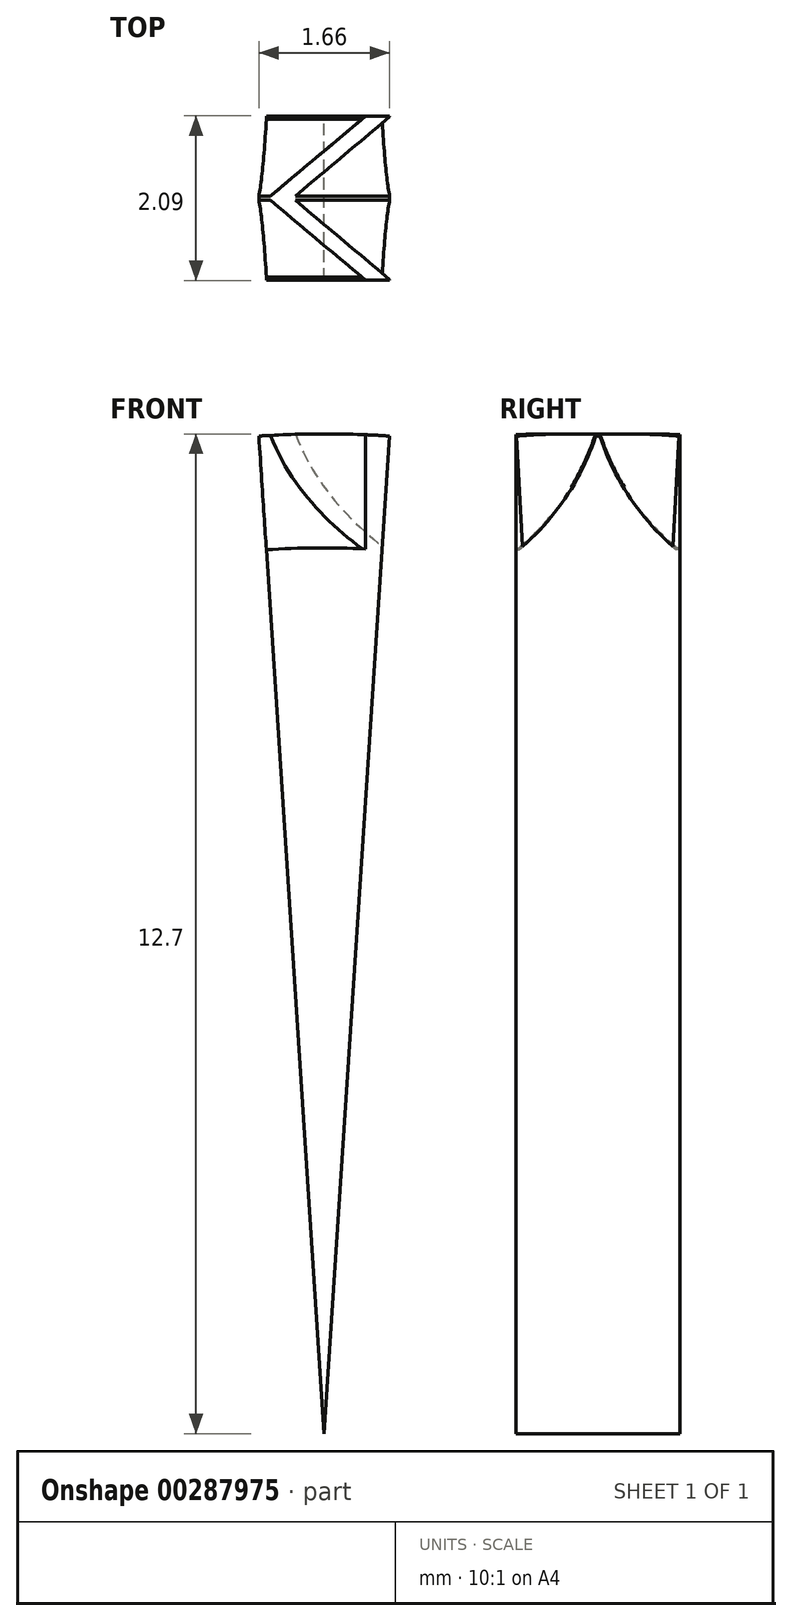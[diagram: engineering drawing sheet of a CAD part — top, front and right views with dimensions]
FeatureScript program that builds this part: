
annotation { "Feature Type Name" : "Feature", "Feature Type Description" : "" }
export const myFeature = defineFeature(function(context is Context, id is Id, definition is map)
    precondition{}
    {
        {
            var Q0;
            Q0=qCreatedBy(makeId("Front.planeOp"),FACE);
            var sketch = newSketch(context, id + "F0", { "sketchPlane" : qUnion([Q0])});
            skLineSegment(sketch, "E0", {"start": v(0, 0) * mm, "end": v(-0.88, 13.46) * mm});
            skLineSegment(sketch, "E1", {"start": v(0, 0) * mm, "end": v(0.88, 13.46) * mm});
            skLineSegment(sketch, "E2", {"start": v(-0.88, 13.46) * mm, "end": v(0.88, 13.46) * mm});
            skSolve(sketch);
        }
        {
            var Q0;
            Q0 = qSketchRegion(id + "F0", true);
            extrude(context, id + "F1", {"entities" : qUnion([Q0]), "depth" : 0.05 * mm, "offsetDistance" : 25.4 * mm});
        }
        {
            var Q0;
            Q0=makeQuery(id+"F1.opExtrude","SWEPT_FACE",FACE,{"disambiguationData":[OSD([sQuery(id+"F0.wireOp",EDGE,"E2")])]});
            var sketch = newSketch(context, id + "F2", { "sketchPlane" : qUnion([Q0])});
            skLineSegment(sketch, "E3", {"start": v(-0.69, 0) * mm, "end": v(0.53, 1.02) * mm});
            skLineSegment(sketch, "E4", {"start": v(0.84, 1.02) * mm, "end": v(-0.37, 0) * mm});
            skLineSegment(sketch, "E5", {"start": v(-0.69, -0.05) * mm, "end": v(0.53, -1.07) * mm});
            skLineSegment(sketch, "E6", {"start": v(0.84, -1.07) * mm, "end": v(-0.37, -0.05) * mm});
            skLineSegment(sketch, "E7", {"start": v(-0.69, 0) * mm, "end": v(-0.37, 0) * mm});
            skLineSegment(sketch, "E8", {"start": v(-0.69, 0) * mm, "end": v(-0.13, 0) * mm});
            skLineSegment(sketch, "E9", {"start": v(-0.37, -0.05) * mm, "end": v(-0.69, -0.05) * mm});
            skLineSegment(sketch, "E10", {"start": v(0.53, 1.02) * mm, "end": v(0.84, 1.02) * mm});
            skLineSegment(sketch, "E11", {"start": v(0.53, -1.07) * mm, "end": v(0.84, -1.07) * mm});
            skPoint(sketch, "E12.orphan", {"position": v(1.16, -1.07) * mm});
            skLineSegment(sketch, "E13", {"start": v(-0.69, 0) * mm, "end": v(-0.69, -0.05) * mm, "construction": true});
            skSolve(sketch);
        }
        {
            var Q0;
            Q0 = qSketchRegion(id + "F2", true);
            extrude(context, id + "F3", {"entities" : qUnion([Q0]), "operationType" : NewBodyOperationType.ADD, "oppositeDirection" : true, "depth" : 2.54 * mm, "offsetDistance" : 25.4 * mm});
        }
        {
            var Q0;
            {var subQ0=sQuery(id+"F0.wireOp",EDGE,"E2");var subQ1=sQuery(id+"F0.wireOp",EDGE,"E1");var subQ2=sQuery(id+"F0.wireOp",EDGE,"E0");var subQ3=makeQuery(id+"F1.opExtrude","CAP_FACE",FACE,{"disambiguationData":[OSD([subQ2,subQ1,subQ0])],"isStart":false});var subQ4=sQuery(id+"F2.wireOp",EDGE,"E5");var subQ5=sQuery(id+"F2.wireOp",EDGE,"E9");var subQ6=sQuery(id+"F2.wireOp",EDGE,"E6");var subQ7=sQuery(id+"F2.wireOp",EDGE,"AgSwT92D-FInu-EsCK-JTKs-pq8kouc3qcbq");Q0=makeQuery(id+"F3.boolean.opBoolean","SPLIT",FACE,{"disambiguationData":[TD([makeQuery(id+"F1.opExtrude","SWEPT_FACE",FACE,{"disambiguationData":[OSD([subQ2])]}),subQ3,makeQuery(id+"F1.opExtrude","SWEPT_FACE",FACE,{"disambiguationData":[OSD([subQ1])]}),makeQuery(id+"F1.opExtrude","SWEPT_FACE",FACE,{"disambiguationData":[OSD([subQ0])]}),makeQuery(id+"F3.opExtrude","CAP_FACE",FACE,{"disambiguationData":[OSD([sQuery(id+"F2.wireOp",EDGE,"E3"),sQuery(id+"F2.wireOp",EDGE,"A9kXBjbS-O0Pt-6HVm-SgFi-jT4OZO6j5QLM"),sQuery(id+"F2.wireOp",EDGE,"E4"),sQuery(id+"F2.wireOp",EDGE,"E8")])],"isStart":true}),makeQuery(id+"F3.opExtrude","SWEPT_FACE",FACE,{"disambiguationData":[OSD([subQ4])]}),makeQuery(id+"F3.opExtrude","CAP_FACE",FACE,{"disambiguationData":[OSD([subQ4,subQ7,subQ6,subQ5])],"isStart":true}),makeQuery(id+"F3.opExtrude","CAP_FACE",FACE,{"disambiguationData":[OSD([subQ4,subQ7,subQ6,subQ5])],"isStart":false}),makeQuery(id+"F3.opExtrude","SWEPT_FACE",FACE,{"disambiguationData":[OSD([subQ6])]})])],"derivedFrom":subQ3});}
            var sketch = newSketch(context, id + "F4", { "sketchPlane" : qUnion([Q0])});
            skCircle(sketch, "E14", {"center": v(0, 0) * mm, "radius": 12.7 * mm});
            skCircle(sketch, "E15", {"center": v(0, 0) * mm, "radius": 16.51 * mm});
            skSolve(sketch);
        }
        {
            var Q0;
            Q0 = qSketchRegion(id + "F4", true);
            extrude(context, id + "F5", {"entities" : qUnion([Q0]), "operationType" : NewBodyOperationType.REMOVE, "oppositeDirection" : true, "depth" : 25.4 * mm});
        }
        {
            var Q0;
            {var subQ0=sQuery(id+"F0.wireOp",EDGE,"E2");var subQ1=sQuery(id+"F0.wireOp",EDGE,"E1");var subQ2=sQuery(id+"F0.wireOp",EDGE,"E0");var subQ3=makeQuery(id+"F1.opExtrude","CAP_FACE",FACE,{"disambiguationData":[OSD([subQ2,subQ1,subQ0])],"isStart":false});var subQ4=sQuery(id+"F2.wireOp",EDGE,"E5");var subQ5=sQuery(id+"F2.wireOp",EDGE,"E9");var subQ6=sQuery(id+"F2.wireOp",EDGE,"E6");var subQ7=sQuery(id+"F2.wireOp",EDGE,"AgSwT92D-FInu-EsCK-JTKs-pq8kouc3qcbq");Q0=makeQuery(id+"F3.boolean.opBoolean","SPLIT",FACE,{"disambiguationData":[TD([makeQuery(id+"F1.opExtrude","SWEPT_FACE",FACE,{"disambiguationData":[OSD([subQ2])]}),subQ3,makeQuery(id+"F1.opExtrude","SWEPT_FACE",FACE,{"disambiguationData":[OSD([subQ1])]}),makeQuery(id+"F1.opExtrude","SWEPT_FACE",FACE,{"disambiguationData":[OSD([subQ0])]}),makeQuery(id+"F3.opExtrude","CAP_FACE",FACE,{"disambiguationData":[OSD([sQuery(id+"F2.wireOp",EDGE,"E3"),sQuery(id+"F2.wireOp",EDGE,"A9kXBjbS-O0Pt-6HVm-SgFi-jT4OZO6j5QLM"),sQuery(id+"F2.wireOp",EDGE,"E4"),sQuery(id+"F2.wireOp",EDGE,"E8")])],"isStart":true}),makeQuery(id+"F3.opExtrude","SWEPT_FACE",FACE,{"disambiguationData":[OSD([subQ4])]}),makeQuery(id+"F3.opExtrude","CAP_FACE",FACE,{"disambiguationData":[OSD([subQ4,subQ7,subQ6,subQ5])],"isStart":true}),makeQuery(id+"F3.opExtrude","CAP_FACE",FACE,{"disambiguationData":[OSD([subQ4,subQ7,subQ6,subQ5])],"isStart":false}),makeQuery(id+"F3.opExtrude","SWEPT_FACE",FACE,{"disambiguationData":[OSD([subQ6])]})])],"derivedFrom":subQ3});}
            var sketch = newSketch(context, id + "F6", { "sketchPlane" : qUnion([Q0])});
            skCircle(sketch, "E16", {"center": v(0, 0) * mm, "radius": 16.51 * mm});
            skCircle(sketch, "E17", {"center": v(0, 0) * mm, "radius": 12.7 * mm});
            skSolve(sketch);
        }
        {
            var Q0;
            Q0 = qSketchRegion(id + "F6", true);
            extrude(context, id + "F7", {"entities" : qUnion([Q0]), "operationType" : NewBodyOperationType.REMOVE, "depth" : 25.4 * mm, "offsetDistance" : 25.4 * mm});
        }
        {
            var Q0;
            {var subQ0=sQuery(id+"F0.wireOp",EDGE,"E2");var subQ1=sQuery(id+"F0.wireOp",EDGE,"E1");var subQ2=sQuery(id+"F0.wireOp",EDGE,"E0");var subQ3=makeQuery(id+"F1.opExtrude","CAP_FACE",FACE,{"disambiguationData":[OSD([subQ2,subQ1,subQ0])],"isStart":false});var subQ4=sQuery(id+"F2.wireOp",EDGE,"E5");var subQ5=sQuery(id+"F2.wireOp",EDGE,"E9");var subQ6=sQuery(id+"F2.wireOp",EDGE,"E6");var subQ7=sQuery(id+"F2.wireOp",EDGE,"AgSwT92D-FInu-EsCK-JTKs-pq8kouc3qcbq");Q0=makeQuery(id+"F3.boolean.opBoolean","SPLIT",FACE,{"disambiguationData":[TD([makeQuery(id+"F1.opExtrude","SWEPT_FACE",FACE,{"disambiguationData":[OSD([subQ2])]}),subQ3,makeQuery(id+"F1.opExtrude","SWEPT_FACE",FACE,{"disambiguationData":[OSD([subQ1])]}),makeQuery(id+"F1.opExtrude","SWEPT_FACE",FACE,{"disambiguationData":[OSD([subQ0])]}),makeQuery(id+"F3.opExtrude","CAP_FACE",FACE,{"disambiguationData":[OSD([sQuery(id+"F2.wireOp",EDGE,"E3"),sQuery(id+"F2.wireOp",EDGE,"A9kXBjbS-O0Pt-6HVm-SgFi-jT4OZO6j5QLM"),sQuery(id+"F2.wireOp",EDGE,"E4"),sQuery(id+"F2.wireOp",EDGE,"E8")])],"isStart":true}),makeQuery(id+"F3.opExtrude","SWEPT_FACE",FACE,{"disambiguationData":[OSD([subQ4])]}),makeQuery(id+"F3.opExtrude","CAP_FACE",FACE,{"disambiguationData":[OSD([subQ4,subQ7,subQ6,subQ5])],"isStart":true}),makeQuery(id+"F3.opExtrude","CAP_FACE",FACE,{"disambiguationData":[OSD([subQ4,subQ7,subQ6,subQ5])],"isStart":false}),makeQuery(id+"F3.opExtrude","SWEPT_FACE",FACE,{"disambiguationData":[OSD([subQ6])]})])],"derivedFrom":subQ3});}
            var sketch = newSketch(context, id + "F8", { "sketchPlane" : qUnion([Q0])});
            skCircle(sketch, "E18", {"center": v(0, 0) * mm, "radius": 11.25 * mm});
            skSolve(sketch);
        }
        {
            var Q0;
            Q0 = qSketchRegion(id + "F8", true);
            extrude(context, id + "F9", {"entities" : qUnion([Q0]), "operationType" : NewBodyOperationType.REMOVE, "depth" : 2.54 * mm, "offsetDistance" : 25.4 * mm});
        }
        {
            var Q0;
            Q0=makeQuery(id+"F1.opExtrude","CAP_FACE",FACE,{"disambiguationData":[OSD([sQuery(id+"F0.wireOp",EDGE,"E0"),sQuery(id+"F0.wireOp",EDGE,"E1"),sQuery(id+"F0.wireOp",EDGE,"E2")])],"isStart":true});
            var sketch = newSketch(context, id + "F10", { "sketchPlane" : qUnion([Q0])});
            skCircle(sketch, "E19", {"center": v(0, 0) * mm, "radius": 11.25 * mm});
            skSolve(sketch);
        }
        {
            var Q0;
            Q0 = qSketchRegion(id + "F10", true);
            extrude(context, id + "F11", {"entities" : qUnion([Q0]), "operationType" : NewBodyOperationType.REMOVE, "depth" : 12.7 * mm, "offsetDistance" : 25.4 * mm});
        }
        {
            var Q0;
            Q0=makeQuery(id+"F11.boolean.opBoolean","MERGE",FACE,{"derivedFrom":[makeQuery(id+"F1.opExtrude","CAP_FACE",FACE,{"disambiguationData":[OSD([sQuery(id+"F0.wireOp",EDGE,"E0"),sQuery(id+"F0.wireOp",EDGE,"E1"),sQuery(id+"F0.wireOp",EDGE,"E2")])],"isStart":true}),makeQuery(id+"F11.opExtrude","CAP_FACE",FACE,{"disambiguationData":[OSD([sQuery(id+"F10.wireOp",EDGE,"E19")])],"isStart":true})]});
            var sketch = newSketch(context, id + "F12", { "sketchPlane" : qUnion([Q0])});
            skArc(sketch, "E20", {"start": v(0.74, 11.23) * mm, "mid": v(0, 11.25) * mm, "end": v(-0.74, 11.23) * mm});
            skLineSegment(sketch, "E21", {"start": v(0, 0) * mm, "end": v(0.74, 11.23) * mm});
            skLineSegment(sketch, "E22", {"start": v(0, 0) * mm, "end": v(-0.74, 11.23) * mm});
            skSolve(sketch);
        }
        {
            var Q0;
            Q0 = qSketchRegion(id + "F12", true);
            extrude(context, id + "F13", {"entities" : qUnion([Q0]), "operationType" : NewBodyOperationType.ADD, "depth" : 1.02 * mm, "offsetDistance" : 25.4 * mm});
        }
        {
            var Q0;
            Q0=makeQuery(id+"F9.boolean.opBoolean","MERGE",FACE,{"derivedFrom":[makeQuery(id+"F1.opExtrude","CAP_FACE",FACE,{"disambiguationData":[OSD([sQuery(id+"F0.wireOp",EDGE,"E0"),sQuery(id+"F0.wireOp",EDGE,"E1"),sQuery(id+"F0.wireOp",EDGE,"E2")])],"isStart":false}),makeQuery(id+"F9.opExtrude","CAP_FACE",FACE,{"disambiguationData":[OSD([sQuery(id+"F8.wireOp",EDGE,"E18")])],"isStart":true})]});
            var sketch = newSketch(context, id + "F14", { "sketchPlane" : qUnion([Q0])});
            skLineSegment(sketch, "E23", {"start": v(0, 0) * mm, "end": v(-0.74, 11.23) * mm});
            skLineSegment(sketch, "E24", {"start": v(0, 0) * mm, "end": v(0.74, 11.23) * mm});
            skArc(sketch, "E25", {"start": v(0.74, 11.23) * mm, "mid": v(0, 11.25) * mm, "end": v(-0.74, 11.23) * mm});
            skSolve(sketch);
        }
        {
            var Q0;
            Q0 = qSketchRegion(id + "F14", true);
            extrude(context, id + "F15", {"entities" : qUnion([Q0]), "operationType" : NewBodyOperationType.ADD, "depth" : 1.02 * mm, "offsetDistance" : 25.4 * mm});
        }
        {
            var Q0;
            Q0=qCreatedBy(makeId("Right.planeOp"),FACE);
            var sketch = newSketch(context, id + "F16", { "sketchPlane" : qUnion([Q0])});
            skArc(sketch, "E26", {"start": v(-1.07, 11.22) * mm, "mid": v(-0.45, 11.89) * mm, "end": v(-0.05, 12.7) * mm});
            skArc(sketch, "E27", {"start": v(0, 12.7) * mm, "mid": v(0.4, 11.89) * mm, "end": v(1.02, 11.22) * mm});
            skLineSegment(sketch, "E28", {"start": v(-1.07, 11.22) * mm, "end": v(1.02, 11.22) * mm});
            skLineSegment(sketch, "E29", {"start": v(-0.05, 12.7) * mm, "end": v(0, 12.7) * mm});
            skSolve(sketch);
        }
        {
            var Q0;
            Q0 = qSketchRegion(id + "F16", true);
            var Q1;
            Q1=makeQuery(id+"F15.boolean.opBoolean","MERGE",EDGE,{"derivedFrom":[makeQuery(id+"F13.boolean.opBoolean","MERGE",EDGE,{"derivedFrom":[makeQuery(id+"F1.opExtrude","SWEPT_EDGE",EDGE,{"disambiguationData":[OSD([sQuery(id+"F0.wireOp",EDGE,"E0"),sQuery(id+"F0.wireOp",EDGE,"E1")])]}),makeQuery(id+"F13.opExtrude","SWEPT_EDGE",EDGE,{"disambiguationData":[OSD([sQuery(id+"F12.wireOp",EDGE,"E21"),sQuery(id+"F12.wireOp",EDGE,"E22")])]})]}),makeQuery(id+"F15.opExtrude","SWEPT_EDGE",EDGE,{"disambiguationData":[OSD([sQuery(id+"F14.wireOp",EDGE,"E23"),sQuery(id+"F14.wireOp",EDGE,"E24")])]})]});
            revolve(context, id + "F17", {"operationType" : NewBodyOperationType.ADD, "entities" : qUnion([Q0]), "axis" : qUnion([Q1]), "revolveType" : RevolveType.FULL});
        }
        {
            var Q0;
            Q0=makeQuery(id+"F15.boolean.opBoolean","MERGE",FACE,{"derivedFrom":[makeQuery(id+"F3.opExtrude","SWEPT_FACE",FACE,{"disambiguationData":[OSD([sQuery(id+"F2.wireOp",EDGE,"E11")])]}),makeQuery(id+"F15.opExtrude","CAP_FACE",FACE,{"disambiguationData":[OSD([sQuery(id+"F14.wireOp",EDGE,"E23"),sQuery(id+"F14.wireOp",EDGE,"E24"),sQuery(id+"F14.wireOp",EDGE,"E25")])],"isStart":false})]});
            var sketch = newSketch(context, id + "F18", { "sketchPlane" : qUnion([Q0])});
            skArc(sketch, "E30", {"start": v(-0.85, 12.93) * mm, "mid": v(0, -12.95) * mm, "end": v(0.85, 12.93) * mm});
            skLineSegment(sketch, "E31", {"start": v(-0.64, 9.8) * mm, "end": v(-0.85, 12.93) * mm});
            skLineSegment(sketch, "E32", {"start": v(0.64, 9.8) * mm, "end": v(0.85, 12.93) * mm});
            skArc(sketch, "E33", {"start": v(-0.64, 9.8) * mm, "mid": v(0, -9.82) * mm, "end": v(0.64, 9.8) * mm});
            skSolve(sketch);
        }
        {
            var Q0;
            Q0 = qSketchRegion(id + "F18", true);
            extrude(context, id + "F19", {"entities" : qUnion([Q0]), "operationType" : NewBodyOperationType.REMOVE, "oppositeDirection" : true, "depth" : 25.4 * mm, "offsetDistance" : 25.4 * mm});
        }
    });
